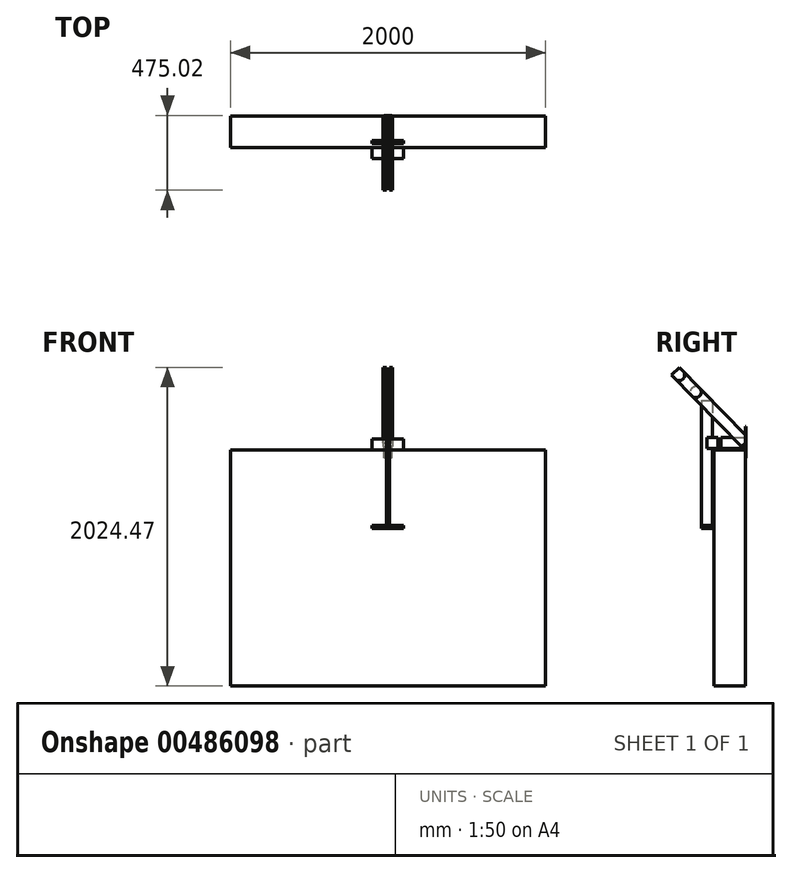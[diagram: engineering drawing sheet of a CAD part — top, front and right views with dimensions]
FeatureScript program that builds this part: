
annotation { "Feature Type Name" : "Feature", "Feature Type Description" : "" }
export const myFeature = defineFeature(function(context is Context, id is Id, definition is map)
    precondition{}
    {
        {
            assignVariable(context, id + "F0", {"name" : "t", "anyValue" : 20 * mm});
        }
        {
            var Q0;
            Q0=qCreatedBy(makeId("Right.planeOp"),FACE);
            var sketch = newSketch(context, id + "F1", { "sketchPlane" : qUnion([Q0])});
            skLineSegment(sketch, "E0", {"start": v(0, 0) * mm, "end": v(0, 1500) * mm});
            skLineSegment(sketch, "E1", {"start": v(0, 1500) * mm, "end": v(200, 1500) * mm});
            skLineSegment(sketch, "E2", {"start": v(200, 1500) * mm, "end": v(200, 0) * mm});
            skLineSegment(sketch, "E3", {"start": v(200, 0) * mm, "end": v(0, 0) * mm});
            skLineSegment(sketch, "E4", {"start": v(-245, 2000) * mm, "end": v(-45, 2000) * mm, "construction": true});
            skLineSegment(sketch, "E5", {"start": v(-45, 2000) * mm, "end": v(-45, 1000) * mm, "construction": true});
            skLineSegment(sketch, "E6", {"start": v(-45, 1545) * mm, "end": v(200, 1545) * mm, "construction": true});
            skLineSegment(sketch, "E7.bottom", {"start": v(200, 1450) * mm, "end": v(205, 1450) * mm});
            skLineSegment(sketch, "E7.top", {"start": v(200, 1650) * mm, "end": v(205, 1650) * mm});
            skLineSegment(sketch, "E7.left", {"start": v(200, 1450) * mm, "end": v(200, 1650) * mm});
            skLineSegment(sketch, "E7.right", {"start": v(205, 1450) * mm, "end": v(205, 1650) * mm});
            skSolve(sketch);
        }
        {
            var Q0;
            Q0=qCreatedBy(makeId("Right.planeOp"),FACE);
            var sketch = newSketch(context, id + "F2", { "sketchPlane" : qUnion([Q0])});
            skLineSegment(sketch, "E8.bottom", {"start": v(-219.98, 2024.47) * mm, "end": v(225.02, 1569.47) * mm});
            skLineSegment(sketch, "E8.top", {"start": v(-270.02, 1975.53) * mm, "end": v(174.98, 1520.53) * mm});
            skLineSegment(sketch, "E8.left", {"start": v(-219.98, 2024.47) * mm, "end": v(-270.02, 1975.53) * mm});
            skLineSegment(sketch, "E8.right", {"start": v(225.02, 1569.47) * mm, "end": v(174.98, 1520.53) * mm});
            skLineSegment(sketch, "E9.bottom", {"start": v(-45, 1510) * mm, "end": v(200, 1510) * mm});
            skLineSegment(sketch, "E9.top", {"start": v(-45, 1580) * mm, "end": v(200, 1580) * mm});
            skLineSegment(sketch, "E9.left", {"start": v(-45, 1580) * mm, "end": v(-45, 1510) * mm});
            skLineSegment(sketch, "E9.right", {"start": v(200, 1580) * mm, "end": v(200, 1510) * mm});
            skLineSegment(sketch, "E10.bottom", {"start": v(-80, 1813.83) * mm, "end": v(-10, 1813.83) * mm});
            skLineSegment(sketch, "E10.top", {"start": v(-80, 1000) * mm, "end": v(-10, 1000) * mm});
            skLineSegment(sketch, "E10.left", {"start": v(-80, 1813.83) * mm, "end": v(-80, 1000) * mm});
            skLineSegment(sketch, "E10.right", {"start": v(-10, 1813.83) * mm, "end": v(-10, 1000) * mm});
            skLineSegment(sketch, "E11.bottom", {"start": v(200, 1580) * mm, "end": v(220, 1580) * mm});
            skLineSegment(sketch, "E11.top", {"start": v(200, 1510) * mm, "end": v(220, 1510) * mm});
            skLineSegment(sketch, "E11.right", {"start": v(220, 1580) * mm, "end": v(220, 1510) * mm});
            skLineSegment(sketch, "E12", {"start": v(200, 1580) * mm, "end": v(200, 1595.06) * mm});
            skLineSegment(sketch, "E13.bottom", {"start": v(25, 1580) * mm, "end": v(45, 1580) * mm});
            skLineSegment(sketch, "E13.top", {"start": v(25, 1500) * mm, "end": v(45, 1500) * mm});
            skLineSegment(sketch, "E13.left", {"start": v(25, 1580) * mm, "end": v(25, 1500) * mm});
            skLineSegment(sketch, "E13.right", {"start": v(45, 1580) * mm, "end": v(45, 1500) * mm});
            skLineSegment(sketch, "E14", {"start": v(25, 1540) * mm, "end": v(45, 1540) * mm});
            skLineSegment(sketch, "E15", {"start": v(25, 1570) * mm, "end": v(45, 1570) * mm});
            skLineSegment(sketch, "E16.bottom", {"start": v(-70, 1020) * mm, "end": v(0, 1020) * mm});
            skLineSegment(sketch, "E16.top", {"start": v(-70, 1000) * mm, "end": v(0, 1000) * mm});
            skLineSegment(sketch, "E16.left", {"start": v(-70, 1020) * mm, "end": v(-70, 1000) * mm});
            skLineSegment(sketch, "E16.right", {"start": v(0, 1020) * mm, "end": v(0, 1000) * mm});
            skLineSegment(sketch, "E17", {"start": v(0, 1010) * mm, "end": v(-80, 1010) * mm, "construction": true});
            skLineSegment(sketch, "E18", {"start": v(-40, 1010) * mm, "end": v(-40, 1000) * mm});
            skLineSegment(sketch, "E19", {"start": v(-40, 1010) * mm, "end": v(-40, 1020) * mm});
            skCircle(sketch, "E20", {"center": v(-220.53, 1974.98) * mm, "radius": 35 * mm});
            skCircle(sketch, "E21", {"center": v(-115, 1867.08) * mm, "radius": 35 * mm});
            skSolve(sketch);
        }
        {
            var Q0;
            Q0=makeQuery(id+"F1.imprint","IMPRINT",FACE,{"disambiguationData":[TD([[makeQuery(id+"F1.imprint","IMPRINT",EDGE,{"derivedFrom":sQuery(id+"F1.wireOp",EDGE,"E0")}),-1.0]])]});
            extrude(context, id + "F3", {"entities" : qUnion([Q0]), "depth" : 2000 * mm, "symmetric" : true});
        }
        {
            var Q0;
            {var subQ5=sQuery(id+"F2.wireOp",EDGE,"E8.left");Q0=makeQuery(id+"F2.imprint","IMPRINT",FACE,{"disambiguationData":[TD([[makeQuery(id+"F2.imprint","IMPRINT",EDGE,{"derivedFrom":subQ5}),1.0]])]});}
            var Q1;
            {var subQ1=sQuery(id+"F2.wireOp",EDGE,"E10.bottom");var subQ5=sQuery(id+"F2.wireOp",EDGE,"E8.bottom");var subQ6=makeQuery(id+"F2.imprint","INTERSECT",VERTEX,{"derivedFrom":[subQ5,subQ1]});Q1=makeQuery(id+"F2.imprint","IMPRINT",FACE,{"disambiguationData":[TD([[makeQuery(id+"F2.imprint","IMPRINT",EDGE,{"disambiguationData":[TD([[subQ6,-1.0]])],"derivedFrom":subQ5}),-1.0]])]});}
            var Q2;
            {var subQ0=sQuery(id+"F2.wireOp",EDGE,"E10.right");var subQ1=sQuery(id+"F2.wireOp",EDGE,"E8.bottom");var subQ2=makeQuery(id+"F2.imprint","INTERSECT",VERTEX,{"derivedFrom":[subQ1,subQ0]});Q2=makeQuery(id+"F2.imprint","IMPRINT",FACE,{"disambiguationData":[TD([[makeQuery(id+"F2.imprint","IMPRINT",EDGE,{"disambiguationData":[TD([[subQ2,-1.0]])],"derivedFrom":subQ1}),-1.0]])]});}
            var Q3;
            {var subQ0=sQuery(id+"F2.wireOp",EDGE,"E8.right");var subQ1=sQuery(id+"F2.wireOp",EDGE,"E8.top");var subQ2=makeQuery(id+"F2.imprint","INTERSECT",VERTEX,{"derivedFrom":[subQ1,subQ0]});Q3=makeQuery(id+"F2.imprint","IMPRINT",FACE,{"disambiguationData":[TD([[makeQuery(id+"F2.imprint","IMPRINT",EDGE,{"disambiguationData":[TD([[subQ2,1.0]])],"derivedFrom":subQ1}),1.0]])]});}
            var Q4;
            {var subQ0=sQuery(id+"F2.wireOp",EDGE,"E20");var subQ1=makeQuery(id+"F2.imprint","INTERSECT",VERTEX,{"derivedFrom":[sQuery(id+"F2.wireOp",EDGE,"E8.bottom"),subQ0]});Q4=makeQuery(id+"F2.imprint","IMPRINT",FACE,{"disambiguationData":[TD([[makeQuery(id+"F2.imprint","IMPRINT",EDGE,{"disambiguationData":[TD([[subQ1,-1.0]])],"derivedFrom":subQ0}),1.0]])]});}
            var Q5;
            {var subQ5=sQuery(id+"F2.wireOp",EDGE,"E20");var subQ7=sQuery(id+"F2.wireOp",EDGE,"E8.bottom");var subQ9=makeQuery(id+"F2.imprint","INTERSECT",VERTEX,{"derivedFrom":[subQ7,subQ5]});Q5=makeQuery(id+"F2.imprint","IMPRINT",FACE,{"disambiguationData":[TD([[makeQuery(id+"F2.imprint","IMPRINT",EDGE,{"disambiguationData":[TD([[subQ9,-1.0]])],"derivedFrom":subQ7}),-1.0]])]});}
            var Q6;
            {var subQ0=sQuery(id+"F2.wireOp",EDGE,"E21");var subQ1=makeQuery(id+"F2.imprint","INTERSECT",VERTEX,{"derivedFrom":[sQuery(id+"F2.wireOp",EDGE,"E8.bottom"),subQ0]});Q6=makeQuery(id+"F2.imprint","IMPRINT",FACE,{"disambiguationData":[TD([[makeQuery(id+"F2.imprint","IMPRINT",EDGE,{"disambiguationData":[TD([[subQ1,-1.0]])],"derivedFrom":subQ0}),1.0]])]});}
            var Q7;
            {var subQ5=sQuery(id+"F2.wireOp",EDGE,"E21");var subQ6=sQuery(id+"F2.wireOp",EDGE,"E8.bottom");var subQ7=makeQuery(id+"F2.imprint","INTERSECT",VERTEX,{"derivedFrom":[subQ6,subQ5]});Q7=makeQuery(id+"F2.imprint","IMPRINT",FACE,{"disambiguationData":[TD([[makeQuery(id+"F2.imprint","IMPRINT",EDGE,{"disambiguationData":[TD([[subQ7,-1.0]])],"derivedFrom":subQ6}),-1.0]])]});}
            extrude(context, id + "F4", {"entities" : qUnion([Q0, Q1, Q2, Q3, Q4, Q5, Q6, Q7]), "depth" : 1.5 * getVariable(context, 't'), "hasSecondDirection" : true, "secondDirectionOppositeDirection" : false, "secondDirectionDepth" : 0.5 * getVariable(context, 't')});
        }
        {
            var Q0;
            Q0=makeQuery(id+"F4.opExtrude","SWEPT_BODY",BODY,{"disambiguationData":[OSD([sQuery(id+"F2.wireOp",EDGE,"E8.bottom"),sQuery(id+"F2.wireOp",EDGE,"E8.top"),sQuery(id+"F2.wireOp",EDGE,"E8.left"),sQuery(id+"F2.wireOp",EDGE,"E8.right")])]});
            var Q1;
            Q1=qCreatedBy(makeId("Right.planeOp"),FACE);
            mirror(context, id + "F5", {"operationType" : NewBodyOperationType.ADD, "entities" : qUnion([Q0]), "mirrorPlane" : qUnion([Q1])});
        }
        {
            var Q0;
            {var subQ0=sQuery(id+"F2.wireOp",EDGE,"E9.left");Q0=makeQuery(id+"F2.imprint","IMPRINT",FACE,{"disambiguationData":[TD([[makeQuery(id+"F2.imprint","IMPRINT",EDGE,{"derivedFrom":subQ0}),-1.0]])]});}
            var Q1;
            {var subQ1=sQuery(id+"F2.wireOp",EDGE,"E10.bottom");var subQ5=sQuery(id+"F2.wireOp",EDGE,"E8.bottom");var subQ6=makeQuery(id+"F2.imprint","INTERSECT",VERTEX,{"derivedFrom":[subQ5,subQ1]});Q1=makeQuery(id+"F2.imprint","IMPRINT",FACE,{"disambiguationData":[TD([[makeQuery(id+"F2.imprint","IMPRINT",EDGE,{"disambiguationData":[TD([[subQ6,-1.0]])],"derivedFrom":subQ5}),-1.0]])]});}
            var Q2;
            {var subQ0=sQuery(id+"F2.wireOp",EDGE,"E16.left");Q2=makeQuery(id+"F2.imprint","IMPRINT",FACE,{"disambiguationData":[TD([[makeQuery(id+"F2.imprint","IMPRINT",EDGE,{"derivedFrom":subQ0}),1.0]])]});}
            var Q3;
            {var subQ0=sQuery(id+"F2.wireOp",EDGE,"E10.bottom");var subQ1=sQuery(id+"F2.wireOp",EDGE,"E8.bottom");var subQ2=makeQuery(id+"F2.imprint","INTERSECT",VERTEX,{"derivedFrom":[subQ1,subQ0]});Q3=makeQuery(id+"F2.imprint","IMPRINT",FACE,{"disambiguationData":[TD([[makeQuery(id+"F2.imprint","IMPRINT",EDGE,{"disambiguationData":[TD([[subQ2,-1.0]])],"derivedFrom":subQ1}),1.0]])]});}
            extrude(context, id + "F6", {"entities" : qUnion([Q0, Q1, Q2, Q3]), "oppositeDirection" : true, "depth" : getVariable(context, 't'), "symmetric" : true});
        }
        {
            var Q0;
            {var subQ3=sQuery(id+"F1.wireOp",EDGE,"E7.bottom");Q0=makeQuery(id+"F1.imprint","IMPRINT",FACE,{"disambiguationData":[TD([[makeQuery(id+"F1.imprint","IMPRINT",EDGE,{"derivedFrom":subQ3}),1.0]])]});}
            extrude(context, id + "F7", {"entities" : qUnion([Q0]), "depth" : 50 * mm, "symmetric" : true});
        }
        {
            var Q0;
            {var subQ1=sQuery(id+"F2.wireOp",EDGE,"E8.top");var subQ9=sQuery(id+"F2.wireOp",EDGE,"E8.right");var subQ10=makeQuery(id+"F2.imprint","INTERSECT",VERTEX,{"derivedFrom":[subQ1,subQ9]});Q0=makeQuery(id+"F2.imprint","IMPRINT",FACE,{"disambiguationData":[TD([[makeQuery(id+"F2.imprint","IMPRINT",EDGE,{"disambiguationData":[TD([[subQ10,1.0]])],"derivedFrom":subQ1}),-1.0]])]});}
            var Q1;
            {var subQ0=sQuery(id+"F2.wireOp",EDGE,"E8.right");var subQ1=sQuery(id+"F2.wireOp",EDGE,"E8.top");var subQ2=makeQuery(id+"F2.imprint","INTERSECT",VERTEX,{"derivedFrom":[subQ1,subQ0]});Q1=makeQuery(id+"F2.imprint","IMPRINT",FACE,{"disambiguationData":[TD([[makeQuery(id+"F2.imprint","IMPRINT",EDGE,{"disambiguationData":[TD([[subQ2,1.0]])],"derivedFrom":subQ1}),1.0]])]});}
            var Q2;
            {var subQ0=sQuery(id+"F2.wireOp",EDGE,"E10.right");var subQ1=sQuery(id+"F2.wireOp",EDGE,"E9.bottom");var subQ2=makeQuery(id+"F2.imprint","INTERSECT",VERTEX,{"derivedFrom":[subQ1,subQ0]});Q2=makeQuery(id+"F2.imprint","IMPRINT",FACE,{"disambiguationData":[TD([[makeQuery(id+"F2.imprint","IMPRINT",EDGE,{"disambiguationData":[TD([[subQ2,-1.0]])],"derivedFrom":subQ1}),1.0]])]});}
            var Q3;
            {var subQ5=sQuery(id+"F2.wireOp",EDGE,"E13.bottom");Q3=makeQuery(id+"F2.imprint","IMPRINT",FACE,{"disambiguationData":[TD([[makeQuery(id+"F2.imprint","IMPRINT",EDGE,{"derivedFrom":subQ5}),-1.0]])]});}
            var Q4;
            {var subQ0=sQuery(id+"F2.wireOp",EDGE,"E9.left");Q4=makeQuery(id+"F2.imprint","IMPRINT",FACE,{"disambiguationData":[TD([[makeQuery(id+"F2.imprint","IMPRINT",EDGE,{"derivedFrom":subQ0}),1.0]])]});}
            extrude(context, id + "F8", {"entities" : qUnion([Q0, Q1, Q2, Q3, Q4]), "depth" : getVariable(context, 't'), "symmetric" : true});
        }
        {
            var Q0;
            {var subQ5=sQuery(id+"F2.wireOp",EDGE,"E13.top");Q0=makeQuery(id+"F2.imprint","IMPRINT",FACE,{"disambiguationData":[TD([[makeQuery(id+"F2.imprint","IMPRINT",EDGE,{"derivedFrom":subQ5}),1.0]])]});}
            var Q1;
            {var subQ5=sQuery(id+"F2.wireOp",EDGE,"E14");Q1=makeQuery(id+"F2.imprint","IMPRINT",FACE,{"disambiguationData":[TD([[makeQuery(id+"F2.imprint","IMPRINT",EDGE,{"derivedFrom":subQ5}),-1.0]])]});}
            var Q2;
            {var subQ0=sQuery(id+"F2.wireOp",EDGE,"E14");Q2=makeQuery(id+"F2.imprint","IMPRINT",FACE,{"disambiguationData":[TD([[makeQuery(id+"F2.imprint","IMPRINT",EDGE,{"derivedFrom":subQ0}),1.0]])]});}
            extrude(context, id + "F9", {"entities" : qUnion([Q0, Q1, Q2]), "depth" : 200 * mm, "symmetric" : true});
        }
        {
            var Q0;
            {var subQ0=sQuery(id+"F2.wireOp",EDGE,"E16.left");Q0=makeQuery(id+"F2.imprint","IMPRINT",FACE,{"disambiguationData":[TD([[makeQuery(id+"F2.imprint","IMPRINT",EDGE,{"derivedFrom":subQ0}),1.0]])]});}
            var Q1;
            {var subQ0=sQuery(id+"F2.wireOp",EDGE,"E18");Q1=makeQuery(id+"F2.imprint","IMPRINT",FACE,{"disambiguationData":[TD([[makeQuery(id+"F2.imprint","IMPRINT",EDGE,{"derivedFrom":subQ0}),1.0]])]});}
            var Q2;
            {var subQ5=sQuery(id+"F2.wireOp",EDGE,"E16.right");Q2=makeQuery(id+"F2.imprint","IMPRINT",FACE,{"disambiguationData":[TD([[makeQuery(id+"F2.imprint","IMPRINT",EDGE,{"derivedFrom":subQ5}),-1.0]])]});}
            extrude(context, id + "F10", {"entities" : qUnion([Q0, Q1, Q2]), "depth" : 200 * mm, "symmetric" : true});
        }
        {
            var Q0;
            Q0=makeQuery(id+"F8.opExtrude","SWEPT_BODY",BODY,{"disambiguationData":[OSD([sQuery(id+"F2.wireOp",EDGE,"E9.bottom"),sQuery(id+"F2.wireOp",EDGE,"E9.top"),sQuery(id+"F2.wireOp",EDGE,"E10.right"),sQuery(id+"F2.wireOp",EDGE,"E9.right"),sQuery(id+"F2.wireOp",EDGE,"E13.bottom"),sQuery(id+"F2.wireOp",EDGE,"E13.left"),sQuery(id+"F2.wireOp",EDGE,"E13.right"),sQuery(id+"F2.wireOp",EDGE,"E14")])]});
            var Q1;
            Q1=makeQuery(id+"F6.opExtrude","SWEPT_BODY",BODY,{"disambiguationData":[OSD([sQuery(id+"F2.wireOp",EDGE,"E8.bottom"),sQuery(id+"F2.wireOp",EDGE,"E9.bottom"),sQuery(id+"F2.wireOp",EDGE,"E9.top"),sQuery(id+"F2.wireOp",EDGE,"E9.left"),sQuery(id+"F2.wireOp",EDGE,"E10.bottom"),sQuery(id+"F2.wireOp",EDGE,"E10.top"),sQuery(id+"F2.wireOp",EDGE,"E10.left"),sQuery(id+"F2.wireOp",EDGE,"E10.right"),sQuery(id+"F2.wireOp",EDGE,"E16.bottom"),sQuery(id+"F2.wireOp",EDGE,"E16.top"),sQuery(id+"F2.wireOp",EDGE,"E18"),sQuery(id+"F2.wireOp",EDGE,"E19")])]});
            var Q2;
            Q2=makeQuery(id+"F9.opExtrude","SWEPT_BODY",BODY,{"disambiguationData":[OSD([sQuery(id+"F2.wireOp",EDGE,"E13.bottom"),sQuery(id+"F2.wireOp",EDGE,"E13.top"),sQuery(id+"F2.wireOp",EDGE,"E13.left"),sQuery(id+"F2.wireOp",EDGE,"E13.right")])]});
            var Q3;
            Q3=makeQuery(id+"F10.opExtrude","SWEPT_BODY",BODY,{"disambiguationData":[OSD([sQuery(id+"F2.wireOp",EDGE,"E16.bottom"),sQuery(id+"F2.wireOp",EDGE,"E16.top"),sQuery(id+"F2.wireOp",EDGE,"E16.left"),sQuery(id+"F2.wireOp",EDGE,"E16.right")])]});
            booleanBodies(context, id + "F11", {"operationType" : BooleanOperationType.SUBTRACTION, "tools" : qUnion([Q0, Q1]), "targets" : qUnion([Q2, Q3]), "keepTools" : true});
        }
        {
            var Q0;
            {var subQ0=sQuery(id+"F2.wireOp",EDGE,"E20");var subQ1=makeQuery(id+"F2.imprint","INTERSECT",VERTEX,{"derivedFrom":[sQuery(id+"F2.wireOp",EDGE,"E8.bottom"),subQ0]});Q0=makeQuery(id+"F2.imprint","IMPRINT",FACE,{"disambiguationData":[TD([[makeQuery(id+"F2.imprint","IMPRINT",EDGE,{"disambiguationData":[TD([[subQ1,-1.0]])],"derivedFrom":subQ0}),1.0]])]});}
            var Q1;
            {var subQ0=sQuery(id+"F2.wireOp",EDGE,"E21");var subQ1=makeQuery(id+"F2.imprint","INTERSECT",VERTEX,{"derivedFrom":[sQuery(id+"F2.wireOp",EDGE,"E8.bottom"),subQ0]});Q1=makeQuery(id+"F2.imprint","IMPRINT",FACE,{"disambiguationData":[TD([[makeQuery(id+"F2.imprint","IMPRINT",EDGE,{"disambiguationData":[TD([[subQ1,-1.0]])],"derivedFrom":subQ0}),1.0]])]});}
            extrude(context, id + "F12", {"entities" : qUnion([Q0, Q1]), "depth" : getVariable(context, 't'), "symmetric" : true});
        }
    });
